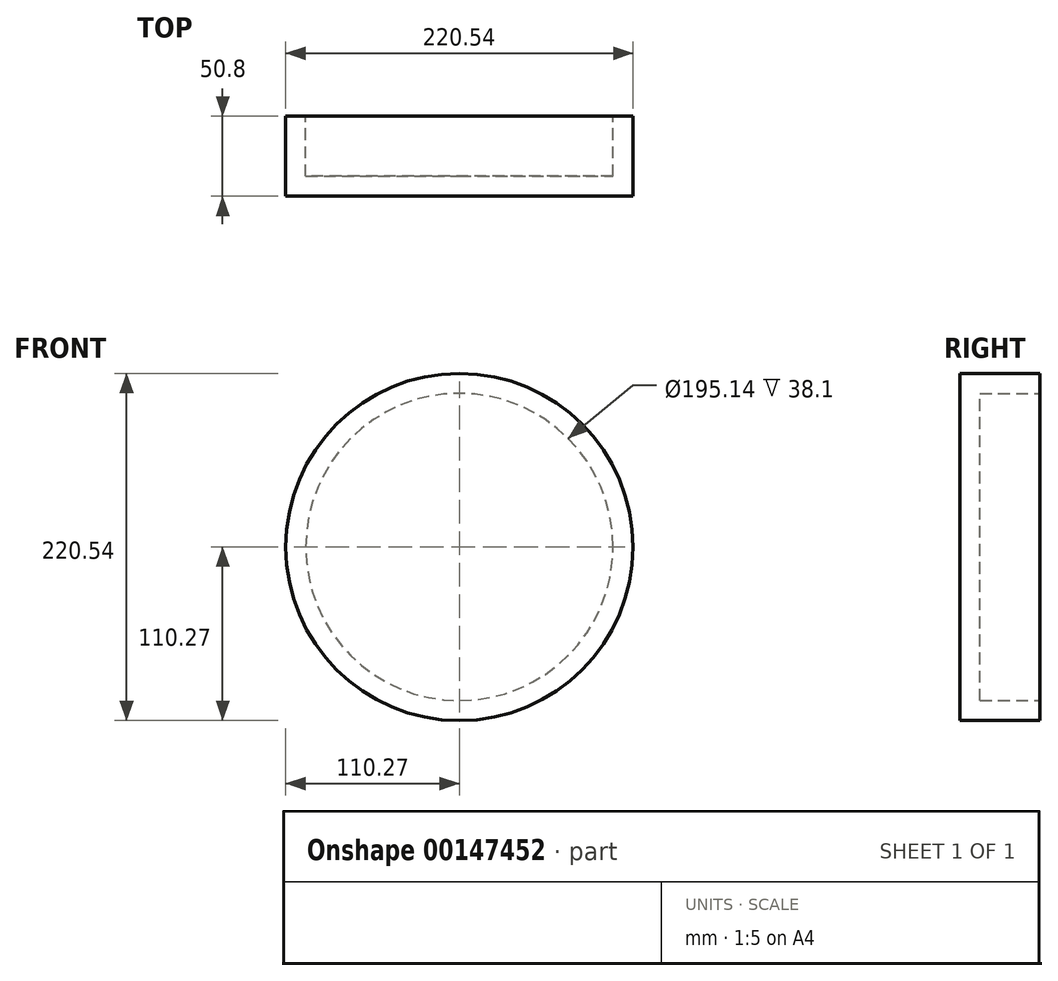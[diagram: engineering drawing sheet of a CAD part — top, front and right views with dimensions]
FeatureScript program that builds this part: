
annotation { "Feature Type Name" : "Feature", "Feature Type Description" : "" }
export const myFeature = defineFeature(function(context is Context, id is Id, definition is map)
    precondition{}
    {
        {
            var Q0;
            Q0=qCreatedBy(makeId("Front.planeOp"),FACE);
            var sketch = newSketch(context, id + "F0", { "sketchPlane" : qUnion([Q0])});
            skCircle(sketch, "E0", {"center": v(0, 0) * mm, "radius": 110.27 * mm});
            skSolve(sketch);
        }
        {
            var Q0;
            Q0=makeQuery(id+"F0.imprint","IMPRINT",FACE,{"disambiguationData":[TD([[makeQuery(id+"F0.imprint","IMPRINT",EDGE,{"derivedFrom":sQuery(id+"F0.wireOp",EDGE,"E0")}),1.0]])]});
            extrude(context, id + "F1", {"entities" : qUnion([Q0]), "depth" : 50.8 * mm});
        }
        {
            var Q0;
            Q0=makeQuery(id+"F1.opExtrude","CAP_FACE",FACE,{"disambiguationData":[OSD([sQuery(id+"F0.wireOp",EDGE,"E0")])],"isStart":true});
            shell(context, id + "F2", {"entities" : qUnion([Q0]), "thickness" : 12.7 * mm});
        }
    });
